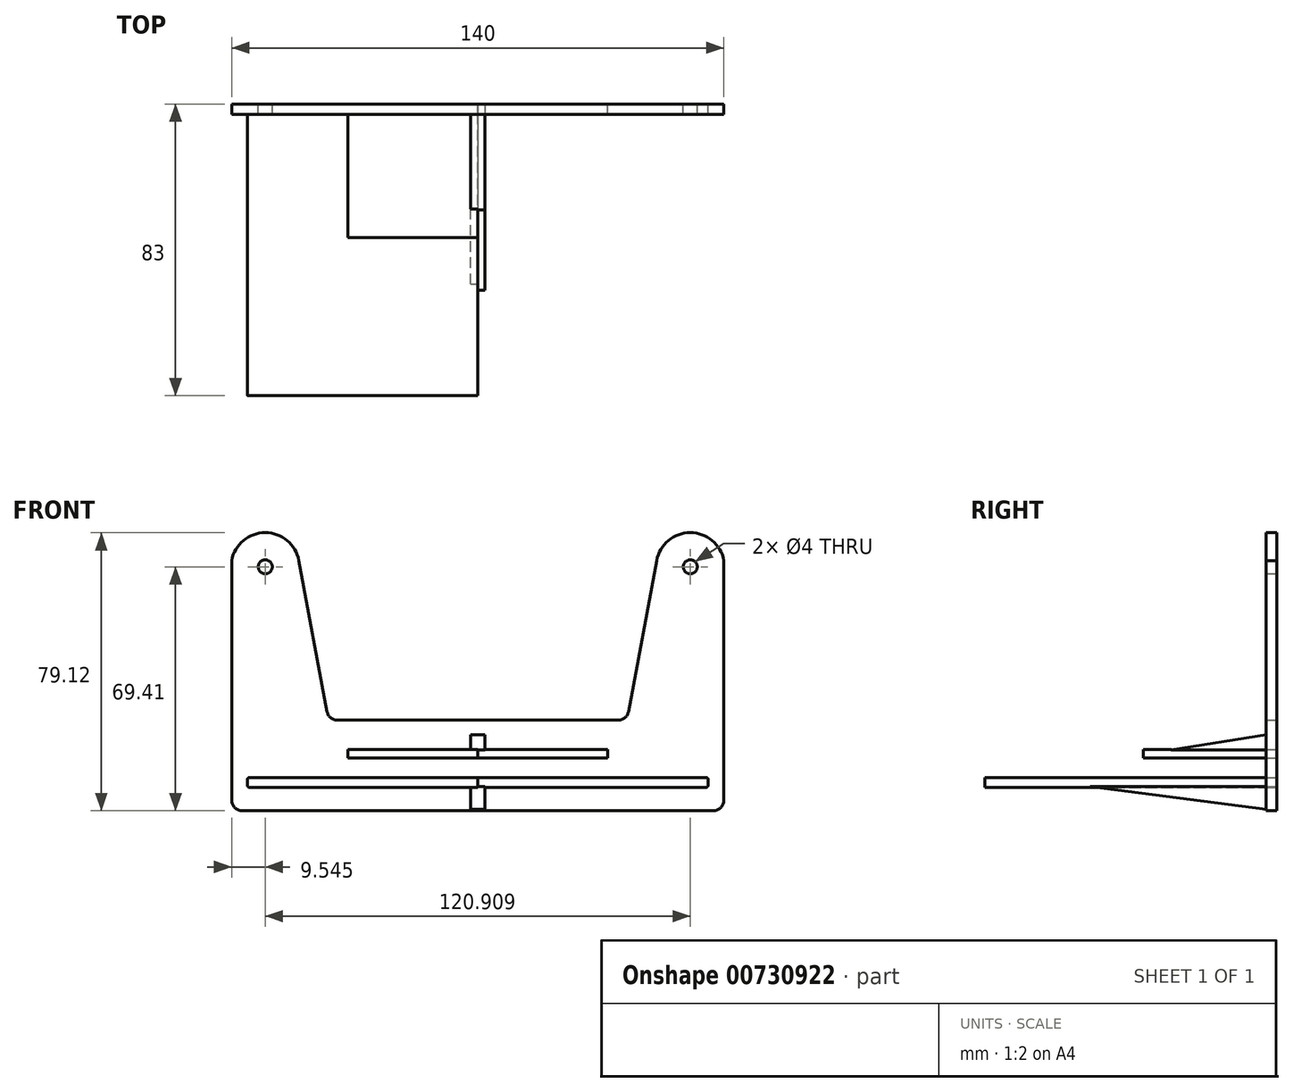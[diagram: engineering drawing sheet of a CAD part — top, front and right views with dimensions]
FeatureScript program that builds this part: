
annotation { "Feature Type Name" : "Feature", "Feature Type Description" : "" }
export const myFeature = defineFeature(function(context is Context, id is Id, definition is map)
    precondition{}
    {
        {
            var Q0;
            Q0=qCreatedBy(makeId("Front.planeOp"),FACE);
            var sketch = newSketch(context, id + "F0", { "sketchPlane" : qUnion([Q0])});
            skLineSegment(sketch, "E0", {"start": v(-70, 3) * mm, "end": v(-70, 71.2) * mm});
            skLineSegment(sketch, "E1", {"start": v(-70, 71.2) * mm, "end": v(-50.9, 71.2) * mm});
            skLineSegment(sketch, "E2", {"start": v(-50.9, 71.2) * mm, "end": v(-42.87, 28.19) * mm});
            skLineSegment(sketch, "E3", {"start": v(-39.92, 25.74) * mm, "end": v(0, 25.74) * mm});
            skLineSegment(sketch, "E4", {"start": v(0, 25.74) * mm, "end": v(0, 0) * mm});
            skLineSegment(sketch, "E5", {"start": v(0, 0) * mm, "end": v(-67, 0) * mm});
            skLineSegment(sketch, "E6.MirrorCS", {"start": v(39.92, 25.74) * mm, "end": v(0, 25.74) * mm});
            skLineSegment(sketch, "E7.MirrorCS", {"start": v(50.9, 71.2) * mm, "end": v(42.87, 28.19) * mm});
            skLineSegment(sketch, "E8.MirrorCS", {"start": v(70, 71.2) * mm, "end": v(50.9, 71.2) * mm});
            skLineSegment(sketch, "E9.MirrorCS", {"start": v(70, 3) * mm, "end": v(70, 71.2) * mm});
            skLineSegment(sketch, "E10.MirrorCS", {"start": v(0, 0) * mm, "end": v(67, 0) * mm});
            skArc(sketch, "E11", {"start": v(-50.9, 71.2) * mm, "mid": v(-60.45, 79.12) * mm, "end": v(-70, 71.2) * mm});
            skArc(sketch, "E12.MirrorCS", {"start": v(50.9, 71.2) * mm, "mid": v(60.45, 79.12) * mm, "end": v(70, 71.2) * mm});
            skPoint(sketch, "E13.visualSharp", {"position": v(-70, 0) * mm});
            skArc(sketch, "E13.filletArc", {"start": v(-70, 3) * mm, "mid": v(-69.12, 0.88) * mm, "end": v(-67, 0) * mm});
            skPoint(sketch, "E14.MirrorP", {"position": v(70, 0) * mm});
            skArc(sketch, "E15.filletArc", {"start": v(67, 0) * mm, "mid": v(69.12, 0.88) * mm, "end": v(70, 3) * mm});
            skPoint(sketch, "E16.visualSharp", {"position": v(-42.41, 25.74) * mm});
            skArc(sketch, "E16.filletArc", {"start": v(-42.87, 28.19) * mm, "mid": v(-41.84, 26.43) * mm, "end": v(-39.92, 25.74) * mm});
            skPoint(sketch, "E17.visualSharp", {"position": v(42.41, 25.74) * mm});
            skArc(sketch, "E17.filletArc", {"start": v(39.92, 25.74) * mm, "mid": v(41.84, 26.43) * mm, "end": v(42.87, 28.19) * mm});
            skLineSegment(sketch, "E18.bottom", {"start": v(-65, 9.46) * mm, "end": v(0, 9.46) * mm});
            skLineSegment(sketch, "E18.top", {"start": v(-65, 6.66) * mm, "end": v(0, 6.66) * mm});
            skLineSegment(sketch, "E18.left", {"start": v(-65.5, 8.96) * mm, "end": v(-65.5, 7.16) * mm});
            skLineSegment(sketch, "E18.right", {"start": v(0, 9.46) * mm, "end": v(0, 6.66) * mm});
            skLineSegment(sketch, "E19.MirrorCS", {"start": v(65, 9.46) * mm, "end": v(0, 9.46) * mm});
            skLineSegment(sketch, "E20.MirrorCS", {"start": v(65.5, 8.96) * mm, "end": v(65.5, 7.16) * mm});
            skLineSegment(sketch, "E21.MirrorCS", {"start": v(65, 6.66) * mm, "end": v(0, 6.66) * mm});
            skPoint(sketch, "E22.visualSharp", {"position": v(-65.5, 9.46) * mm});
            skArc(sketch, "E22.filletArc", {"start": v(-65, 9.46) * mm, "mid": v(-65.35, 9.31) * mm, "end": v(-65.5, 8.96) * mm});
            skPoint(sketch, "E23.visualSharp", {"position": v(-65.5, 6.66) * mm});
            skArc(sketch, "E23.filletArc", {"start": v(-65.5, 7.16) * mm, "mid": v(-65.35, 6.8) * mm, "end": v(-65, 6.66) * mm});
            skPoint(sketch, "E24.visualSharp", {"position": v(65.5, 9.46) * mm});
            skArc(sketch, "E24.filletArc", {"start": v(65.5, 8.96) * mm, "mid": v(65.35, 9.31) * mm, "end": v(65, 9.46) * mm});
            skPoint(sketch, "E25.visualSharp", {"position": v(65.5, 6.66) * mm});
            skArc(sketch, "E25.filletArc", {"start": v(65, 6.66) * mm, "mid": v(65.35, 6.8) * mm, "end": v(65.5, 7.16) * mm});
            skLineSegment(sketch, "E26.bottom", {"start": v(0, 17.36) * mm, "end": v(-37, 17.36) * mm});
            skLineSegment(sketch, "E26.top", {"start": v(0, 14.96) * mm, "end": v(-37, 14.96) * mm});
            skLineSegment(sketch, "E26.left", {"start": v(0, 17.36) * mm, "end": v(0, 14.96) * mm});
            skLineSegment(sketch, "E26.right", {"start": v(-37, 17.36) * mm, "end": v(-37, 14.96) * mm});
            skLineSegment(sketch, "E27.MirrorCS", {"start": v(0, 17.36) * mm, "end": v(37, 17.36) * mm});
            skLineSegment(sketch, "E28.MirrorCS", {"start": v(37, 17.36) * mm, "end": v(37, 14.96) * mm});
            skLineSegment(sketch, "E29.MirrorCS", {"start": v(0, 14.96) * mm, "end": v(37, 14.96) * mm});
            skSolve(sketch);
        }
        {
            var Q0;
            Q0=makeQuery(id+"F0.imprint","IMPRINT",FACE,{"disambiguationData":[TD([[makeQuery(id+"F0.imprint","IMPRINT",EDGE,{"derivedFrom":sQuery(id+"F0.wireOp",EDGE,"E18.bottom")}),-1.0]])]});
            var Q1;
            Q1=makeQuery(id+"F0.imprint","IMPRINT",FACE,{"disambiguationData":[TD([[makeQuery(id+"F0.imprint","IMPRINT",EDGE,{"derivedFrom":sQuery(id+"F0.wireOp",EDGE,"E18.right")}),1.0]])]});
            extrude(context, id + "F1", {"entities" : qUnion([Q0, Q1]), "depth" : 83 * mm, "offsetDistance" : 25 * mm});
        }
        {
            var Q0;
            Q0=makeQuery(id+"F0.imprint","IMPRINT",FACE,{"disambiguationData":[TD([[makeQuery(id+"F0.imprint","IMPRINT",EDGE,{"derivedFrom":sQuery(id+"F0.wireOp",EDGE,"E26.bottom")}),1.0]])]});
            var Q1;
            Q1=makeQuery(id+"F0.imprint","IMPRINT",FACE,{"disambiguationData":[TD([[makeQuery(id+"F0.imprint","IMPRINT",EDGE,{"derivedFrom":sQuery(id+"F0.wireOp",EDGE,"E26.left")}),1.0]])]});
            extrude(context, id + "F2", {"entities" : qUnion([Q0, Q1]), "depth" : 38 * mm, "offsetDistance" : 25 * mm});
        }
        {
            var Q0;
            Q0=makeQuery(id+"F0.imprint","IMPRINT",FACE,{"disambiguationData":[TD([[makeQuery(id+"F0.imprint","IMPRINT",EDGE,{"derivedFrom":sQuery(id+"F0.wireOp",EDGE,"E1")}),1.0]])]});
            var Q1;
            Q1=makeQuery(id+"F0.imprint","IMPRINT",FACE,{"disambiguationData":[TD([[makeQuery(id+"F0.imprint","IMPRINT",EDGE,{"derivedFrom":sQuery(id+"F0.wireOp",EDGE,"E8.MirrorCS")}),-1.0]])]});
            var Q2;
            {var subQ2=sQuery(id+"F0.wireOp",EDGE,"E6.MirrorCS");Q2=makeQuery(id+"F0.imprint","IMPRINT",FACE,{"disambiguationData":[TD([[makeQuery(id+"F0.imprint","IMPRINT",EDGE,{"derivedFrom":subQ2}),1.0]])]});}
            var Q3;
            Q3=makeQuery(id+"F0.imprint","IMPRINT",FACE,{"disambiguationData":[TD([[makeQuery(id+"F0.imprint","IMPRINT",EDGE,{"derivedFrom":sQuery(id+"F0.wireOp",EDGE,"E0")}),-1.0]])]});
            extrude(context, id + "F3", {"entities" : qUnion([Q0, Q1, Q2, Q3]), "operationType" : NewBodyOperationType.ADD, "depth" : 3 * mm, "offsetDistance" : 25 * mm});
        }
        {
            var Q0;
            Q0=sQuery(id+"F0.wireOp",VERTEX,"E11.center");
            var Q1;
            Q1=makeQuery(id+"F1.opExtrude","SWEPT_BODY",BODY,{"disambiguationData":[OSD([sQuery(id+"F0.wireOp",EDGE,"E18.bottom"),sQuery(id+"F0.wireOp",EDGE,"E18.top"),sQuery(id+"F0.wireOp",EDGE,"E18.left"),sQuery(id+"F0.wireOp",EDGE,"E19.MirrorCS"),sQuery(id+"F0.wireOp",EDGE,"E20.MirrorCS"),sQuery(id+"F0.wireOp",EDGE,"E21.MirrorCS"),sQuery(id+"F0.wireOp",EDGE,"E22.filletArc"),sQuery(id+"F0.wireOp",EDGE,"E23.filletArc"),sQuery(id+"F0.wireOp",EDGE,"E24.filletArc"),sQuery(id+"F0.wireOp",EDGE,"E25.filletArc")])]});
            hole(context, id + "F4", {"style" : HoleStyle.SIMPLE, "endStyle" : HoleEndStyle.THROUGH, "oppositeDirection" : true, "holeDiameter" : 4 * mm, "majorDiameter" : 5 * mm, "isTappedThrough" : true, "tappedDepth" : 12 * mm, "tapClearance" : 3, "locations" : qUnion([Q0]), "scope" : qUnion([Q1])});
        }
        {
            var Q0;
            Q0=sQuery(id+"F0.wireOp",VERTEX,"E12.MirrorCS.center");
            var Q1;
            Q1=makeQuery(id+"F1.opExtrude","SWEPT_BODY",BODY,{"disambiguationData":[OSD([sQuery(id+"F0.wireOp",EDGE,"E18.bottom"),sQuery(id+"F0.wireOp",EDGE,"E18.top"),sQuery(id+"F0.wireOp",EDGE,"E18.left"),sQuery(id+"F0.wireOp",EDGE,"E19.MirrorCS"),sQuery(id+"F0.wireOp",EDGE,"E20.MirrorCS"),sQuery(id+"F0.wireOp",EDGE,"E21.MirrorCS"),sQuery(id+"F0.wireOp",EDGE,"E22.filletArc"),sQuery(id+"F0.wireOp",EDGE,"E23.filletArc"),sQuery(id+"F0.wireOp",EDGE,"E24.filletArc"),sQuery(id+"F0.wireOp",EDGE,"E25.filletArc")])]});
            hole(context, id + "F5", {"style" : HoleStyle.SIMPLE, "endStyle" : HoleEndStyle.THROUGH, "oppositeDirection" : true, "holeDiameter" : 4 * mm, "majorDiameter" : 5 * mm, "isTappedThrough" : true, "tappedDepth" : 12 * mm, "tapClearance" : 3, "locations" : qUnion([Q0]), "scope" : qUnion([Q1])});
        }
        {
            var Q0;
            Q0=qCreatedBy(makeId("Right.planeOp"),FACE);
            var sketch = newSketch(context, id + "F6", { "sketchPlane" : qUnion([Q0])});
            skLineSegment(sketch, "E30", {"start": v(0, 0) * mm, "end": v(-53.06, 6.9) * mm});
            skLineSegment(sketch, "E31", {"start": v(-53.06, 6.9) * mm, "end": v(0, 6.9) * mm});
            skLineSegment(sketch, "E32", {"start": v(0, 6.9) * mm, "end": v(0, 0) * mm});
            skLineSegment(sketch, "E33", {"start": v(-2.96, 17.33) * mm, "end": v(-2.96, 21.65) * mm});
            skLineSegment(sketch, "E34", {"start": v(-2.96, 21.65) * mm, "end": v(-30.12, 17.33) * mm});
            skLineSegment(sketch, "E35", {"start": v(-30.12, 17.33) * mm, "end": v(-2.96, 17.33) * mm});
            skSolve(sketch);
        }
        {
            var Q0;
            Q0=makeQuery(id+"F6.imprint","IMPRINT",FACE,{"disambiguationData":[TD([[makeQuery(id+"F6.imprint","IMPRINT",EDGE,{"derivedFrom":sQuery(id+"F6.wireOp",EDGE,"E30")}),-1.0]])]});
            extrude(context, id + "F7", {"entities" : qUnion([Q0]), "operationType" : NewBodyOperationType.ADD, "endBound" : BoundingType.SYMMETRIC, "depth" : 4 * mm, "offsetDistance" : 25 * mm});
        }
        {
            var Q0;
            Q0=makeQuery(id+"F6.imprint","IMPRINT",FACE,{"disambiguationData":[TD([[makeQuery(id+"F6.imprint","IMPRINT",EDGE,{"derivedFrom":sQuery(id+"F6.wireOp",EDGE,"E33")}),1.0]])]});
            extrude(context, id + "F8", {"entities" : qUnion([Q0]), "operationType" : NewBodyOperationType.ADD, "endBound" : BoundingType.SYMMETRIC, "depth" : 4 * mm, "offsetDistance" : 25 * mm});
        }
        {
            var Q0;
            Q0=makeQuery(id+"F2.opExtrude","SWEPT_FACE",FACE,{"disambiguationData":[OSD([sQuery(id+"F0.wireOp",EDGE,"E26.bottom"),sQuery(id+"F0.wireOp",EDGE,"E27.MirrorCS")])]});
            var sketch = newSketch(context, id + "F9", { "sketchPlane" : qUnion([Q0])});
            skPoint(sketch, "E36", {"position": v(32, -33) * mm});
            skSolve(sketch);
        }
        {
            var Q0;
            Q0=sQuery(id+"F9.wireOp",VERTEX,"E36");
            var Q1;
            Q1=makeQuery(id+"F1.opExtrude","SWEPT_BODY",BODY,{"disambiguationData":[OSD([sQuery(id+"F0.wireOp",EDGE,"E18.bottom"),sQuery(id+"F0.wireOp",EDGE,"E18.top"),sQuery(id+"F0.wireOp",EDGE,"E18.left"),sQuery(id+"F0.wireOp",EDGE,"E19.MirrorCS"),sQuery(id+"F0.wireOp",EDGE,"E20.MirrorCS"),sQuery(id+"F0.wireOp",EDGE,"E21.MirrorCS"),sQuery(id+"F0.wireOp",EDGE,"E22.filletArc"),sQuery(id+"F0.wireOp",EDGE,"E23.filletArc"),sQuery(id+"F0.wireOp",EDGE,"E24.filletArc"),sQuery(id+"F0.wireOp",EDGE,"E25.filletArc")])]});
            hole(context, id + "F10", {"style" : HoleStyle.SIMPLE, "endStyle" : HoleEndStyle.THROUGH, "holeDiameter" : 2 * mm, "majorDiameter" : 5 * mm, "isTappedThrough" : true, "tappedDepth" : 12 * mm, "tapClearance" : 3, "locations" : qUnion([Q0]), "scope" : qUnion([Q1])});
        }
    });
